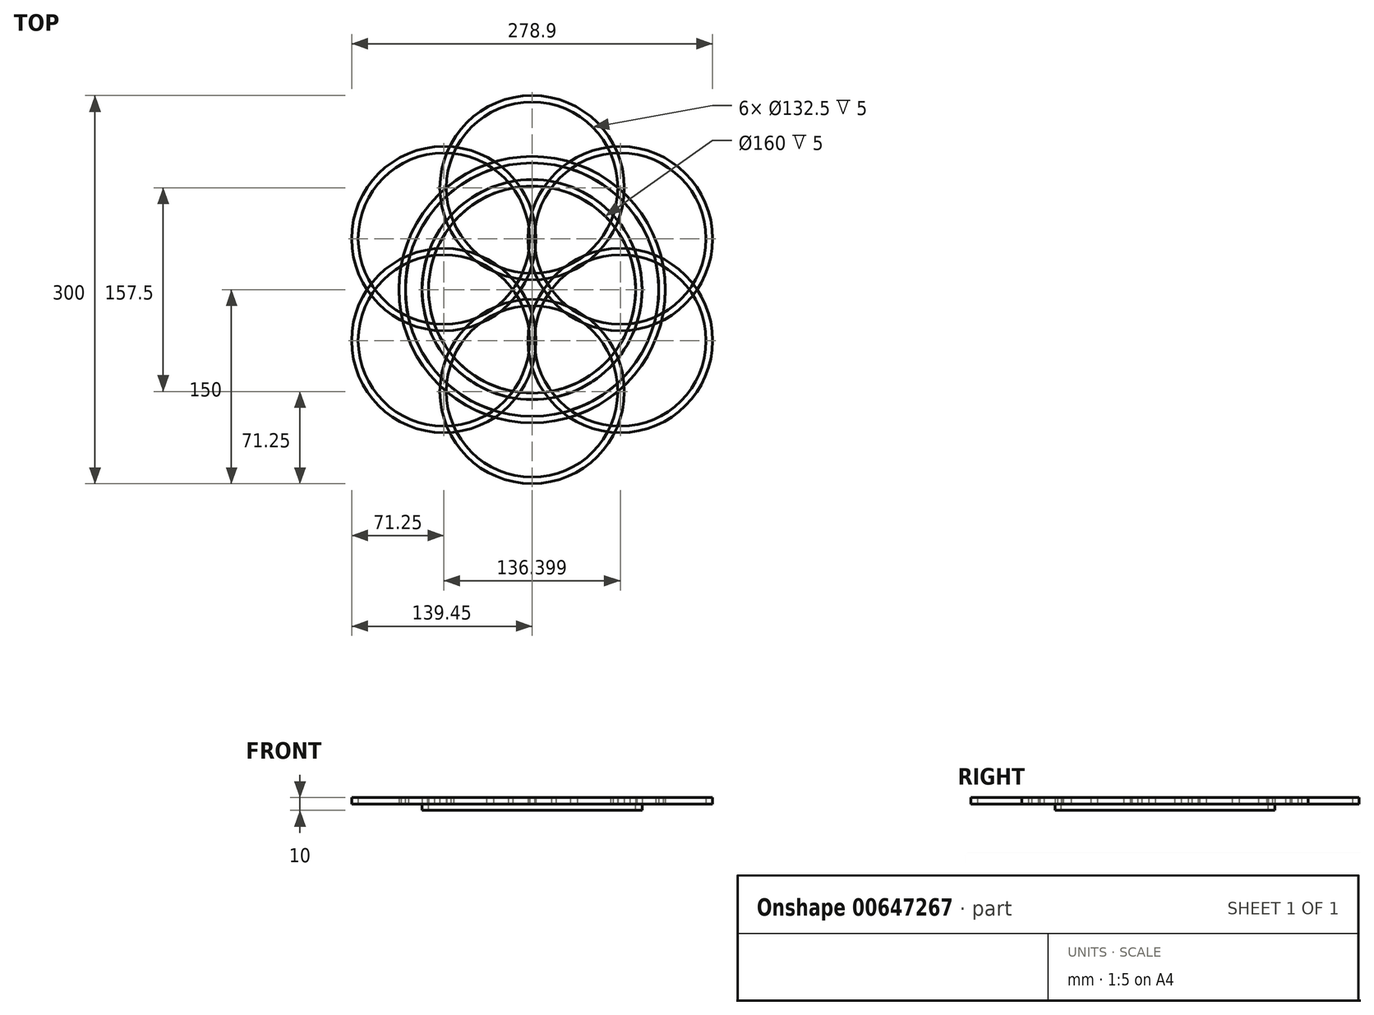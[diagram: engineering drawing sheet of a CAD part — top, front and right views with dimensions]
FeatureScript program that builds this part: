
annotation { "Feature Type Name" : "Feature", "Feature Type Description" : "" }
export const myFeature = defineFeature(function(context is Context, id is Id, definition is map)
    precondition{}
    {
        {
            var Q0;
            Q0=qCreatedBy(makeId("Top.planeOp"),FACE);
            var sketch = newSketch(context, id + "F0", { "sketchPlane" : qUnion([Q0])});
            skCircle(sketch, "E0", {"center": v(0, 0) * mm, "radius": 150 * mm, "construction": true});
            skLineSegment(sketch, "E1.bottom", {"start": v(-150, 150) * mm, "end": v(150, 150) * mm, "construction": true});
            skLineSegment(sketch, "E1.top", {"start": v(-150, -150) * mm, "end": v(150, -150) * mm, "construction": true});
            skLineSegment(sketch, "E1.left", {"start": v(-150, 150) * mm, "end": v(-150, -150) * mm, "construction": true});
            skLineSegment(sketch, "E1.right", {"start": v(150, 150) * mm, "end": v(150, -150) * mm, "construction": true});
            skCircle(sketch, "E2", {"center": v(0, 0) * mm, "radius": 7.5 * mm, "construction": true});
            skCircle(sketch, "E3", {"center": v(0, 0) * mm, "radius": 85 * mm});
            skCircle(sketch, "E4", {"center": v(0, 0) * mm, "radius": 80 * mm});
            skCircle(sketch, "E5", {"center": v(0, 78.75) * mm, "radius": 71.25 * mm});
            skCircle(sketch, "E6", {"center": v(0, 78.75) * mm, "radius": 66.25 * mm});
            skArc(sketch, "E7", {"start": v(-71.12, 74.38) * mm, "mid": v(0, -102.91) * mm, "end": v(71.12, 74.38) * mm, "construction": true});
            skPoint(sketch, "E7.first.point", {"position": v(-66.25, 78.75) * mm});
            skPoint(sketch, "E7.second.point", {"position": v(66.25, 78.75) * mm});
            skPoint(sketch, "E7.third.point", {"position": v(19.23, -101.1) * mm});
            skArc(sketch, "E8.0", {"start": v(-70.44, 68) * mm, "mid": v(0, -97.91) * mm, "end": v(70.44, 68) * mm, "construction": true});
            skArc(sketch, "E9.trimOffspring", {"start": v(65.94, 72.37) * mm, "mid": v(0, 97.91) * mm, "end": v(-65.94, 72.37) * mm});
            skArc(sketch, "E10.trimOffspring", {"start": v(66.25, 78.75) * mm, "mid": v(0, 102.91) * mm, "end": v(-66.25, 78.75) * mm});
            skSolve(sketch);
        }
        {
            var Q0;
            {var subQ0=sQuery(id+"F0.wireOp",EDGE,"E5");var subQ1=sQuery(id+"F0.wireOp",EDGE,"E3");var subQ2=makeQuery(id+"F0.imprint","INTERSECT",VERTEX,{"disambiguationData":[OD(0.0)],"derivedFrom":[subQ1,subQ0]});Q0=makeQuery(id+"F0.imprint","IMPRINT",FACE,{"disambiguationData":[TD([[makeQuery(id+"F0.imprint","IMPRINT",EDGE,{"disambiguationData":[TD([[subQ2,1.0]])],"derivedFrom":subQ1}),1.0]])]});}
            var Q1;
            {var subQ0=sQuery(id+"F0.wireOp",EDGE,"E5");var subQ1=sQuery(id+"F0.wireOp",EDGE,"E3");var subQ2=makeQuery(id+"F0.imprint","INTERSECT",VERTEX,{"disambiguationData":[OD(1.0)],"derivedFrom":[subQ1,subQ0]});Q1=makeQuery(id+"F0.imprint","IMPRINT",FACE,{"disambiguationData":[TD([[makeQuery(id+"F0.imprint","IMPRINT",EDGE,{"disambiguationData":[TD([[subQ2,1.0]])],"derivedFrom":subQ1}),1.0]])]});}
            var Q2;
            {var subQ0=sQuery(id+"F0.wireOp",EDGE,"E6");var subQ1=sQuery(id+"F0.wireOp",EDGE,"E3");var subQ2=makeQuery(id+"F0.imprint","INTERSECT",VERTEX,{"disambiguationData":[OD(0.0)],"derivedFrom":[subQ1,subQ0]});Q2=makeQuery(id+"F0.imprint","IMPRINT",FACE,{"disambiguationData":[TD([[makeQuery(id+"F0.imprint","IMPRINT",EDGE,{"disambiguationData":[TD([[subQ2,-1.0]])],"derivedFrom":subQ1}),1.0]])]});}
            var Q3;
            {var subQ0=sQuery(id+"F0.wireOp",EDGE,"E5");var subQ1=sQuery(id+"F0.wireOp",EDGE,"E3");var subQ2=makeQuery(id+"F0.imprint","INTERSECT",VERTEX,{"disambiguationData":[OD(0.0)],"derivedFrom":[subQ1,subQ0]});Q3=makeQuery(id+"F0.imprint","IMPRINT",FACE,{"disambiguationData":[TD([[makeQuery(id+"F0.imprint","IMPRINT",EDGE,{"disambiguationData":[TD([[subQ2,-1.0]])],"derivedFrom":subQ1}),1.0]])]});}
            extrude(context, id + "F1", {"entities" : qUnion([Q0, Q1, Q2, Q3]), "oppositeDirection" : true, "depth" : 5 * mm, "offsetDistance" : 25 * mm});
        }
        {
            var Q0;
            {var subQ0=sQuery(id+"F0.wireOp",EDGE,"E5");var subQ1=sQuery(id+"F0.wireOp",EDGE,"E3");var subQ2=makeQuery(id+"F0.imprint","INTERSECT",VERTEX,{"disambiguationData":[OD(0.0)],"derivedFrom":[subQ1,subQ0]});Q0=makeQuery(id+"F0.imprint","IMPRINT",FACE,{"disambiguationData":[TD([[makeQuery(id+"F0.imprint","IMPRINT",EDGE,{"disambiguationData":[TD([[subQ2,-1.0]])],"derivedFrom":subQ1}),-1.0]])]});}
            var Q1;
            {var subQ0=sQuery(id+"F0.wireOp",EDGE,"E5");var subQ1=sQuery(id+"F0.wireOp",EDGE,"E3");var subQ2=makeQuery(id+"F0.imprint","INTERSECT",VERTEX,{"disambiguationData":[OD(1.0)],"derivedFrom":[subQ1,subQ0]});Q1=makeQuery(id+"F0.imprint","IMPRINT",FACE,{"disambiguationData":[TD([[makeQuery(id+"F0.imprint","IMPRINT",EDGE,{"disambiguationData":[TD([[subQ2,1.0]])],"derivedFrom":subQ1}),1.0]])]});}
            var Q2;
            {var subQ0=sQuery(id+"F0.wireOp",EDGE,"E6");var subQ1=sQuery(id+"F0.wireOp",EDGE,"E4");var subQ2=makeQuery(id+"F0.imprint","INTERSECT",VERTEX,{"disambiguationData":[OD(0.0)],"derivedFrom":[subQ1,subQ0]});Q2=makeQuery(id+"F0.imprint","IMPRINT",FACE,{"disambiguationData":[TD([[makeQuery(id+"F0.imprint","IMPRINT",EDGE,{"disambiguationData":[TD([[subQ2,1.0]])],"derivedFrom":subQ1}),1.0]])]});}
            var Q3;
            {var subQ0=sQuery(id+"F0.wireOp",EDGE,"E5");var subQ1=sQuery(id+"F0.wireOp",EDGE,"E3");var subQ2=makeQuery(id+"F0.imprint","INTERSECT",VERTEX,{"disambiguationData":[OD(0.0)],"derivedFrom":[subQ1,subQ0]});Q3=makeQuery(id+"F0.imprint","IMPRINT",FACE,{"disambiguationData":[TD([[makeQuery(id+"F0.imprint","IMPRINT",EDGE,{"disambiguationData":[TD([[subQ2,-1.0]])],"derivedFrom":subQ1}),1.0]])]});}
            extrude(context, id + "F2", {"entities" : qUnion([Q0, Q1, Q2, Q3]), "depth" : 5 * mm, "offsetDistance" : 25 * mm});
        }
        {
            var Q0;
            {var subQ0=sQuery(id+"F0.wireOp",EDGE,"E9.trimOffspring");Q0=makeQuery(id+"F0.imprint","IMPRINT",FACE,{"disambiguationData":[TD([[makeQuery(id+"F0.imprint","IMPRINT",EDGE,{"derivedFrom":subQ0}),-1.0]])]});}
            var Q1;
            {var subQ0=sQuery(id+"F0.wireOp",EDGE,"E6");var subQ1=sQuery(id+"F0.wireOp",EDGE,"E3");var subQ2=makeQuery(id+"F0.imprint","INTERSECT",VERTEX,{"disambiguationData":[OD(0.0)],"derivedFrom":[subQ1,subQ0]});Q1=makeQuery(id+"F0.imprint","IMPRINT",FACE,{"disambiguationData":[TD([[makeQuery(id+"F0.imprint","IMPRINT",EDGE,{"disambiguationData":[TD([[subQ2,-1.0]])],"derivedFrom":subQ1}),1.0]])]});}
            extrude(context, id + "F3", {"entities" : qUnion([Q0, Q1]), "depth" : 5 * mm, "offsetDistance" : 25 * mm});
        }
        {
            var Q0;
            Q0=makeQuery(id+"F2.opExtrude","SWEPT_BODY",BODY,{"disambiguationData":[OSD([sQuery(id+"F0.wireOp",EDGE,"E5"),sQuery(id+"F0.wireOp",EDGE,"E6")])]});
            var Q1;
            Q1=makeQuery(id+"F3.opExtrude","SWEPT_BODY",BODY,{"disambiguationData":[OSD([sQuery(id+"F0.wireOp",EDGE,"E6"),sQuery(id+"F0.wireOp",EDGE,"E9.trimOffspring"),sQuery(id+"F0.wireOp",EDGE,"E10.trimOffspring")])]});
            var Q2;
            Q2=makeQuery(id+"F3.opExtrude","SWEPT_BODY",BODY,{"disambiguationData":[OSD([sQuery(id+"F0.wireOp",EDGE,"E3"),sQuery(id+"F0.wireOp",EDGE,"E4"),sQuery(id+"F0.wireOp",EDGE,"E6")])]});
            var Q3;
            Q3=sQuery(id+"F0.wireOp",EDGE,"E3");
            circularPattern(context, id + "F4", {"entities" : qUnion([Q0, Q1, Q2]), "axis" : qUnion([Q3]), "angle" : 360 * degree, "instanceCount" : 6, "equalSpace" : true});
        }
    });
